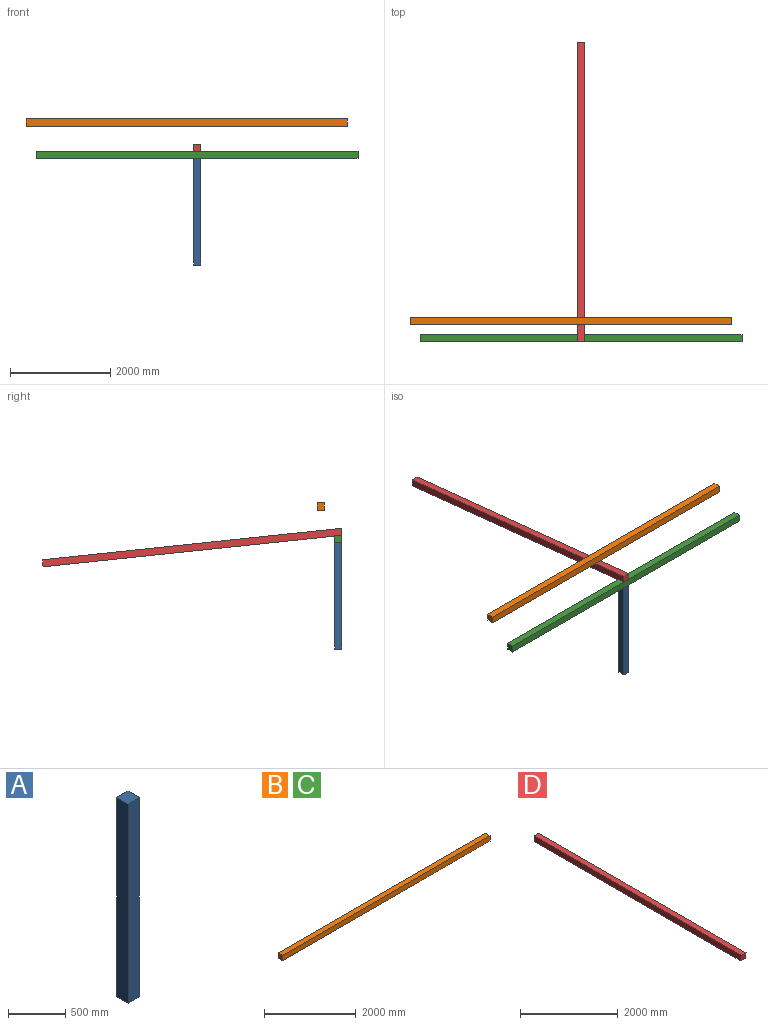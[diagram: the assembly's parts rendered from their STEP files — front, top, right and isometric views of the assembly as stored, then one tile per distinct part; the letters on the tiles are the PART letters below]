
ASSEMBLY  parts=4 mates=2
PART A: 6 faces, bbox 140x140x2125 mm
  f0: plane 2125x140mm, normal (-1,0,0), area 297500mm2, adj f1,f3,f4,f5
  f1: plane 2125x140mm, normal (0,-1,0), area 297500mm2, adj f0,f2,f4,f5
  f2: plane 2125x140mm, normal (1,0,0), area 297500mm2, adj f1,f3,f4,f5
  f3: plane 2125x140mm, normal (0,1,0), area 297500mm2, adj f0,f2,f4,f5
  f4: plane 140x140mm, normal (0,0,1), area 19600mm2, adj f0,f1,f2,f3
  f5: plane 140x140mm, normal (0,0,-1), area 19600mm2, adj f0,f1,f2,f3
PART B: 6 faces, bbox 6400x140x140 mm
  f0: plane 6400x140mm, normal (0,0,1), area 896000mm2, adj f1,f3,f4,f5
  f1: plane 6400x140mm, normal (0,-1,0), area 896000mm2, adj f0,f2,f4,f5
  f2: plane 6400x140mm, normal (0,0,-1), area 896000mm2, adj f1,f3,f4,f5
  f3: plane 6400x140mm, normal (0,1,0), area 896000mm2, adj f0,f2,f4,f5
  f4: plane 140x140mm, normal (1,0,0), area 19600mm2, adj f0,f1,f2,f3
  f5: plane 140x140mm, normal (-1,0,0), area 19600mm2, adj f0,f1,f2,f3
PART C: same geometry as B
PART D: 8 faces, bbox 140x6000x140 mm
  f0: plane 6000x140mm, normal (1,0,0), area 837940mm2, adj f2,f3,f4,f5,f6,f7
  f1: plane 6000x140mm, normal (-1,0,0), area 837940mm2, adj f2,f3,f4,f5,f6,f7
  f2: plane 5844.51x140mm, normal (0,0,-1), area 818232mm2, adj f0,f1,f4,f7
  f3: plane 6000x140mm, normal (0,0,1), area 840000mm2, adj f0,f1,f4,f5
  f4: plane 140x140mm, normal (0,1,0), area 19600mm2, adj f0,f1,f2,f3
  f5: plane 140x140mm, normal (0,-0.99,-0.1), area 19708mm2, adj f0,f1,f3,f6
  f6: plane 140x139.23mm, normal (0,0.1,-0.99), area 19600mm2, adj f0,f1,f5,f7
  f7: plane 140x14.63mm, normal (0,-0.99,-0.1), area 2060mm2, adj f0,f1,f2,f6
PLACE A at identity
PLACE B t=(-3347.88,345.09,2910.6)mm
PLACE C t=(-3130,0,2265)mm
PLACE D rot(axis=(-1,0,0),6deg) t=(0,-14.63,2266.54)mm
MATE planar D.f6 <-> C.f0  axis (0,0,-1) through (70,70,2265)mm
MATE planar C.f2 <-> A.f4  axis (0,0,-1) through (70,70,2125)mm
